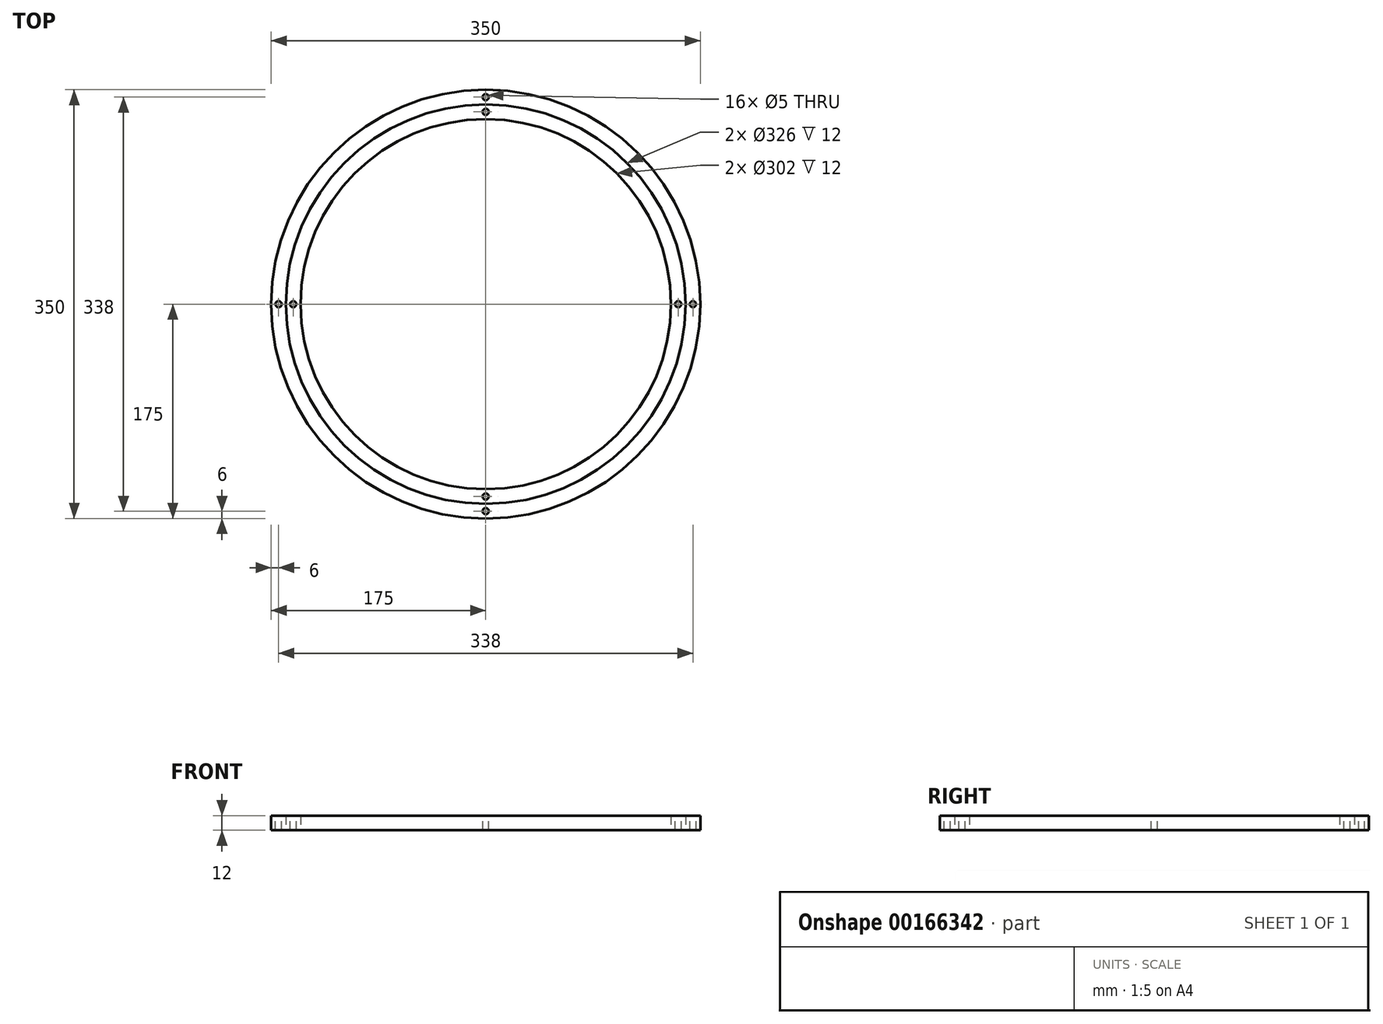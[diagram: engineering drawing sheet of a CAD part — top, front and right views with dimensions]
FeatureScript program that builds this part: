
annotation { "Feature Type Name" : "Feature", "Feature Type Description" : "" }
export const myFeature = defineFeature(function(context is Context, id is Id, definition is map)
    precondition{}
    {
        {
            var Q0;
            Q0=qCreatedBy(makeId("Top.planeOp"),FACE);
            var sketch = newSketch(context, id + "F0", { "sketchPlane" : qUnion([Q0])});
            skCircle(sketch, "E0", {"center": v(0, 0) * mm, "radius": 175 * mm});
            skCircle(sketch, "E1", {"center": v(0, 0) * mm, "radius": 163 * mm});
            skSolve(sketch);
        }
        {
            var Q0;
            Q0=makeQuery(id+"F0.imprint","IMPRINT",FACE,{"disambiguationData":[TD([[makeQuery(id+"F0.imprint","IMPRINT",EDGE,{"derivedFrom":sQuery(id+"F0.wireOp",EDGE,"E0")}),1.0]])]});
            extrude(context, id + "F1", {"entities" : qUnion([Q0]), "depth" : 12 * mm});
        }
        {
            var Q0;
            Q0=qCreatedBy(makeId("Top.planeOp"),FACE);
            var sketch = newSketch(context, id + "F2", { "sketchPlane" : qUnion([Q0])});
            skCircle(sketch, "E2", {"center": v(0, 0) * mm, "radius": 163 * mm});
            skCircle(sketch, "E3", {"center": v(0, 0) * mm, "radius": 151 * mm});
            skSolve(sketch);
        }
        {
            var Q0;
            Q0=qSketchRegion(id+"F2",true);
            extrude(context, id + "F3", {"entities" : qUnion([Q0]), "depth" : 12 * mm});
        }
        {
            var Q0;
            Q0=makeQuery(id+"F3.opExtrude","CAP_FACE",FACE,{"disambiguationData":[OSD([sQuery(id+"F2.wireOp",EDGE,"E2"),sQuery(id+"F2.wireOp",EDGE,"E3")])],"isStart":false});
            var sketch = newSketch(context, id + "F4", { "sketchPlane" : qUnion([Q0])});
            skLineSegment(sketch, "E4", {"start": v(0, 0) * mm, "end": v(0, 157) * mm});
            skCircle(sketch, "E5", {"center": v(0, 157) * mm, "radius": 2.5 * mm});
            skCircle(sketch, "E6.1.0", {"center": v(-157, 0) * mm, "radius": 2.5 * mm});
            skCircle(sketch, "E6.2.0", {"center": v(0, -157) * mm, "radius": 2.5 * mm});
            skCircle(sketch, "E6.3.0", {"center": v(157, 0) * mm, "radius": 2.5 * mm});
            skPoint(sketch, "E6.center", {"position": v(0, 0) * mm});
            skSolve(sketch);
        }
        {
            var Q0;
            Q0=qSketchRegion(id+"F4",true);
            extrude(context, id + "F5", {"entities" : qUnion([Q0]), "operationType" : NewBodyOperationType.REMOVE, "oppositeDirection" : true, "depth" : 12 * mm});
        }
        {
            var Q0;
            Q0=makeQuery(id+"F1.opExtrude","CAP_FACE",FACE,{"disambiguationData":[OSD([sQuery(id+"F0.wireOp",EDGE,"E0"),sQuery(id+"F0.wireOp",EDGE,"E1")])],"isStart":false});
            var sketch = newSketch(context, id + "F6", { "sketchPlane" : qUnion([Q0])});
            skLineSegment(sketch, "E7", {"start": v(0, 0) * mm, "end": v(0, 169) * mm});
            skCircle(sketch, "E8", {"center": v(0, 169) * mm, "radius": 2.5 * mm});
            skCircle(sketch, "E9.1.0", {"center": v(-169, 0) * mm, "radius": 2.5 * mm});
            skCircle(sketch, "E9.2.0", {"center": v(0, -169) * mm, "radius": 2.5 * mm});
            skCircle(sketch, "E9.3.0", {"center": v(169, 0) * mm, "radius": 2.5 * mm});
            skPoint(sketch, "E9.center", {"position": v(0, 0) * mm});
            skSolve(sketch);
        }
        {
            var Q0;
            Q0 = qSketchRegion(id + "F6", true);
            extrude(context, id + "F7", {"entities" : qUnion([Q0]), "operationType" : NewBodyOperationType.REMOVE, "oppositeDirection" : true, "depth" : 12 * mm});
        }
    });
